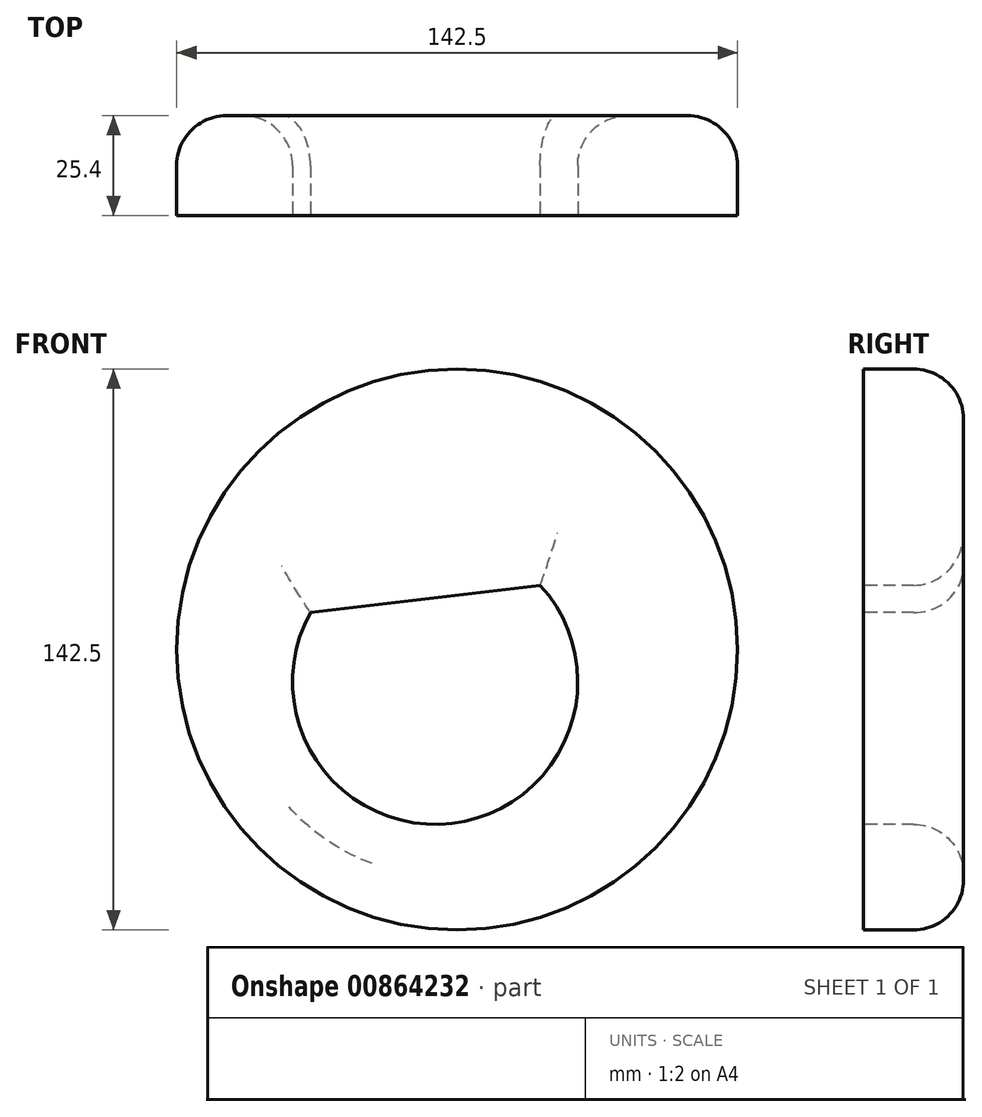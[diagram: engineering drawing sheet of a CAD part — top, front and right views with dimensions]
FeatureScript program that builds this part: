
annotation { "Feature Type Name" : "Feature", "Feature Type Description" : "" }
export const myFeature = defineFeature(function(context is Context, id is Id, definition is map)
    precondition{}
    {
        {
            var Q0;
            Q0=qCreatedBy(makeId("Front.planeOp"),FACE);
            var sketch = newSketch(context, id + "F0", { "sketchPlane" : qUnion([Q0])});
            skCircle(sketch, "E0", {"center": v(0, 0) * mm, "radius": 71.25 * mm});
            skSolve(sketch);
        }
        {
            var Q0;
            Q0=makeQuery(id+"F0.imprint","IMPRINT",FACE,{"disambiguationData":[TD([[makeQuery(id+"F0.imprint","IMPRINT",EDGE,{"derivedFrom":sQuery(id+"F0.wireOp",EDGE,"E0")}),1.0]])]});
            extrude(context, id + "F1", {"entities" : qUnion([Q0]), "depth" : 25.4 * mm, "offsetDistance" : 25.4 * mm});
        }
        {
            var Q0;
            Q0=makeQuery(id+"F1.opExtrude","CAP_FACE",FACE,{"disambiguationData":[OSD([sQuery(id+"F0.wireOp",EDGE,"E0")])],"isStart":false});
            var sketch = newSketch(context, id + "F2", { "sketchPlane" : qUnion([Q0])});
            skArc(sketch, "E1", {"start": v(-37.27, 9.36) * mm, "mid": v(-1.3, -44.16) * mm, "end": v(21.1, 16.32) * mm});
            skLineSegment(sketch, "E2", {"start": v(-37.27, 9.36) * mm, "end": v(21.1, 16.32) * mm});
            skSolve(sketch);
        }
        {
            var Q0;
            Q0=makeQuery(id+"F2.imprint","IMPRINT",FACE,{"disambiguationData":[TD([[makeQuery(id+"F2.imprint","IMPRINT",EDGE,{"derivedFrom":sQuery(id+"F2.wireOp",EDGE,"E1")}),1.0]])]});
            extrude(context, id + "F3", {"entities" : qUnion([Q0]), "operationType" : NewBodyOperationType.REMOVE, "endBound" : BoundingType.THROUGH_ALL, "oppositeDirection" : true, "depth" : 25.4 * mm, "offsetDistance" : 25.4 * mm});
        }
        {
            var Q0;
            Q0=makeQuery(id+"F1.opExtrude","CAP_EDGE",EDGE,{"disambiguationData":[OSD([sQuery(id+"F0.wireOp",EDGE,"E0")])],"isStart":true});
            var Q1;
            Q1=makeQuery(id+"F3.boolean.opBoolean","INTERSECT",EDGE,{"derivedFrom":[makeQuery(id+"F1.opExtrude","CAP_FACE",FACE,{"disambiguationData":[OSD([sQuery(id+"F0.wireOp",EDGE,"E0")])],"isStart":true}),makeQuery(id+"F3.opExtrude","SWEPT_FACE",FACE,{"disambiguationData":[OSD([sQuery(id+"F2.wireOp",EDGE,"E2")])]})]});
            var Q2;
            Q2=makeQuery(id+"F3.boolean.opBoolean","INTERSECT",EDGE,{"derivedFrom":[makeQuery(id+"F1.opExtrude","CAP_FACE",FACE,{"disambiguationData":[OSD([sQuery(id+"F0.wireOp",EDGE,"E0")])],"isStart":true}),makeQuery(id+"F3.opExtrude","SWEPT_FACE",FACE,{"disambiguationData":[OSD([sQuery(id+"F2.wireOp",EDGE,"E1")])]})]});
            fillet(context, id + "F4", {"entities" : qUnion([Q0, Q1, Q2]), "radius" : 12.7 * mm, "tangentPropagation" : true, "allowEdgeOverflow" : false});
        }
    });
